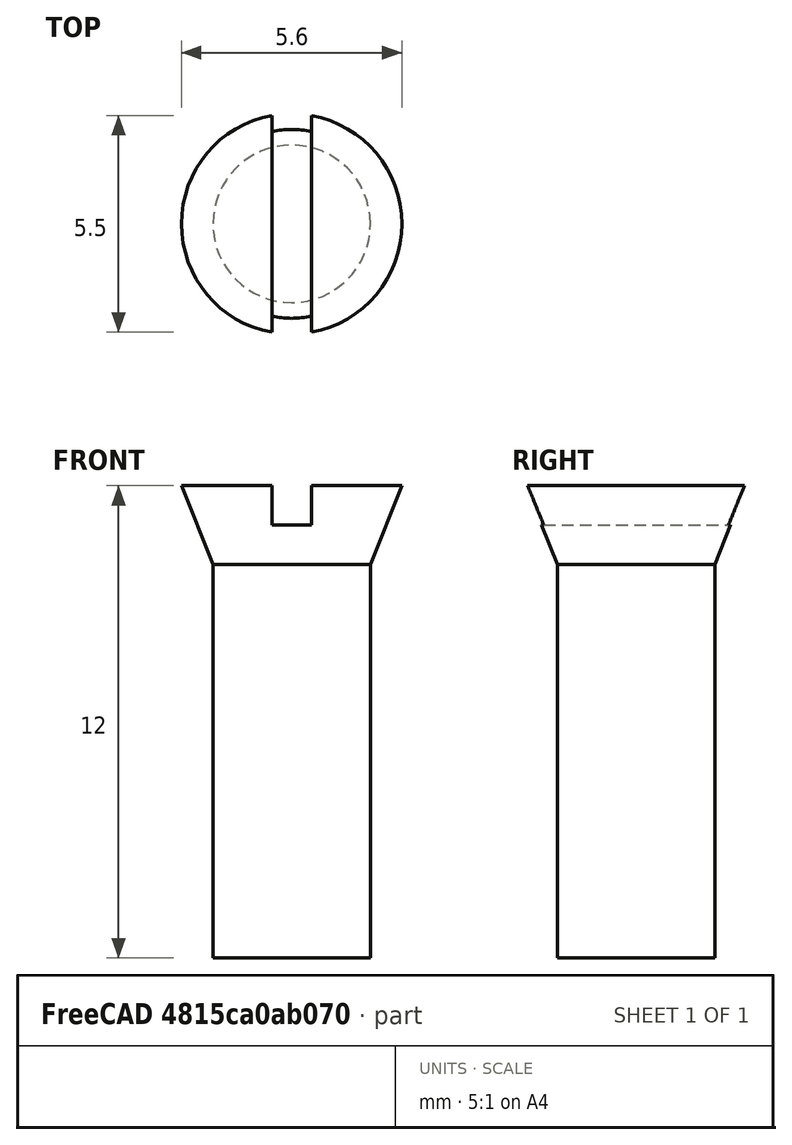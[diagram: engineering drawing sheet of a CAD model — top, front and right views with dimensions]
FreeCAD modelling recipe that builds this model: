
FCSTD DOCUMENT  (FreeCAD 1.0R39319 (Git))
Label: ojt1_t14r01_screw
License: All rights reserved
LicenseURL: https://en.wikipedia.org/wiki/All_rights_reserved
objects: Part::Cylinder×1, Part::Cone×1, Part::MultiFuse×1, Part::Box×1, Part::Cut×1
note: 5 computed .brp shape members not serialized (recipe doc carries the construction recipe); baked Part::Feature solids carry a one-line shape summary decoded from their .brp

FEATURE [Part::Cylinder] Cylinder  label="Cilindre"
  Angle = 360
  AttacherType = Attacher::AttachEngine3D
  FirstAngle = 0
  Height = 10
  Radius = 2
  SecondAngle = 0
FEATURE [Part::Cone] Cone  label="Con"
  Angle = 360
  AttacherType = Attacher::AttachEngine3D
  Height = 2
  Placement = pos=(0,0,10) rot=(0,0,1;0rad)
  Radius1 = 2
  Radius2 = 2.8
FEATURE [Part::MultiFuse] Fusion
  Refine = true
  Shapes = -> [Cone,Cylinder]
FEATURE [Part::Box] Box  label="Cub"
  AttacherType = Attacher::AttachEngine3D
  Height = 4
  Length = 1
  Placement = pos=(-0.5,-6,11) rot=(0,0,1;0rad)
  Width = 10
FEATURE [Part::Cut] Cut
  Base = -> Fusion
  Refine = true
  Tool = -> Box
